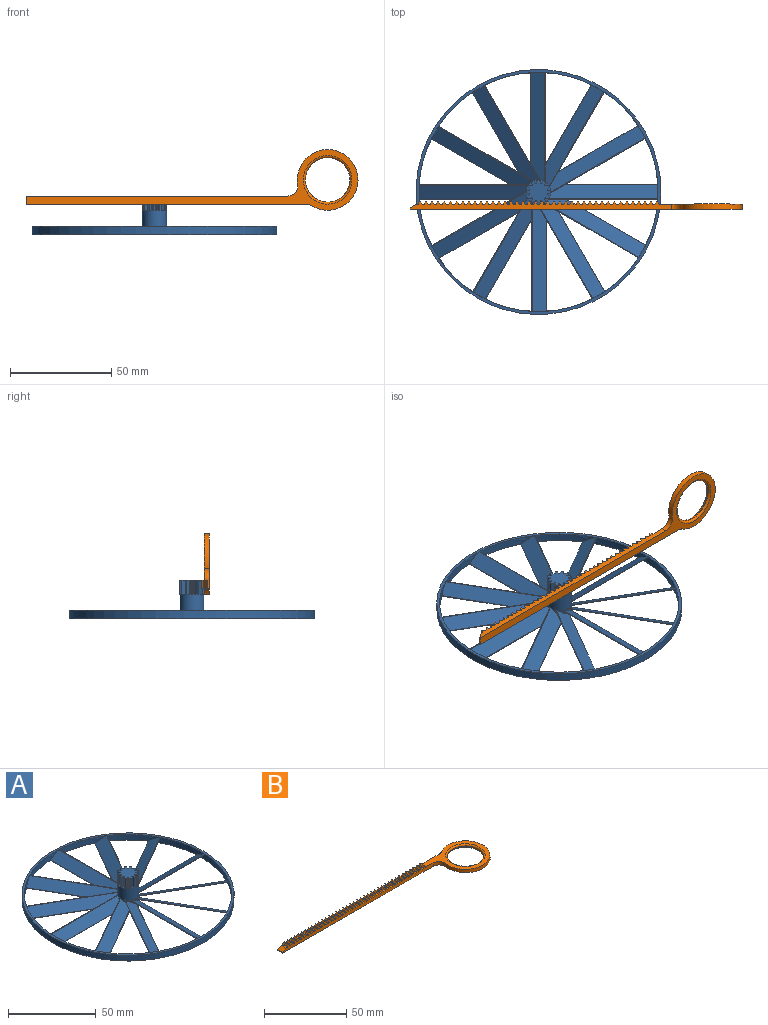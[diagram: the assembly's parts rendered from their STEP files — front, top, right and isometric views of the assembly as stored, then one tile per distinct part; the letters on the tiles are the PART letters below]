
ASSEMBLY  parts=2 mates=1
PART A: 92 faces, bbox 121.1x121.1x19.1 mm
  f0: plane 2.1x1.71mm, normal (0,0,1), area 2.1mm2, adj f12,f56,f59,f90
  f1: plane 1.96x1.96mm, normal (0,0,1), area 2.1mm2, adj f12,f87,f89,f91
  f2: plane 2.1x1.71mm, normal (0,0,1), area 2.1mm2, adj f12,f84,f86,f88
  f3: plane 2.1x1.71mm, normal (0,0,1), area 2.1mm2, adj f12,f81,f83,f85
  f4: plane 1.96x1.96mm, normal (0,0,1), area 2.1mm2, adj f12,f78,f80,f82
  f5: plane 2.1x1.71mm, normal (0,0,1), area 2.1mm2, adj f12,f75,f77,f79
  f6: plane 2.1x1.71mm, normal (0,0,1), area 2.1mm2, adj f12,f72,f74,f76
  f7: plane 1.96x1.96mm, normal (0,0,1), area 2.1mm2, adj f12,f69,f71,f73
  f8: plane 2.1x1.71mm, normal (0,0,1), area 2.1mm2, adj f12,f66,f68,f70
  f9: plane 2.1x1.71mm, normal (0,0,1), area 2.1mm2, adj f12,f63,f65,f67
  f10: plane 1.96x1.96mm, normal (0,0,1), area 2.1mm2, adj f12,f60,f62,f64
  f11: plane 2.1x1.71mm, normal (0,0,1), area 2.1mm2, adj f12,f55,f58,f61
  f12: cylinder r=6mm len=19mm, axis (0,0,-1), area 479.2mm2, adj f0,f1,f2,f3,f4,f5,f6,f7
  f13: cylinder r=6mm len=0.68mm, axis (0,0,-1), area 0.1mm2, adj f12,f16,f34
  f14: cylinder r=6mm len=3.6mm, axis (0,0,-1), area 2.4mm2, adj f12,f16,f35,f36
  f15: cylinder r=6mm len=5.58mm, axis (0,0,-1), area 6.1mm2, adj f12,f16,f37,f38
  f16: plane 121x121mm, normal (0,0,-1), area 866.8mm2, adj f12,f13,f14,f15,f17,f18,f19,f20
  f17: cylinder r=20mm len=54.2mm, axis (0,1,0), area 430.3mm2, adj f12,f16,f41,f54
  f18: plane 54.47x6.93mm, normal (0.5,0,0.87), area 427.4mm2, adj f12,f16,f42,f54
  f19: cylinder r=20mm len=50.4mm, axis (-0.5,0.87,0), area 430.3mm2, adj f12,f16,f42,f54
  f20: plane 50.1x33.19mm, normal (0.43,-0.25,0.87), area 427.4mm2, adj f12,f16,f41,f54
  f21: plane 50.57x32.93mm, normal (0.43,0.25,0.87), area 427.4mm2, adj f12,f16,f43,f54
  f22: cylinder r=20mm len=50.4mm, axis (-0.87,0.5,0), area 430.3mm2, adj f12,f16,f43,f54
  f23: plane 50.1x33.19mm, normal (0.25,0.43,0.87), area 427.4mm2, adj f12,f16,f44,f54
  f24: cylinder r=20mm len=54.2mm, axis (-1,0,0), area 430.3mm2, adj f12,f16,f44,f54
  f25: plane 54.47x6.93mm, normal (0,0.5,0.87), area 427.4mm2, adj f12,f16,f45,f54
  f26: cylinder r=20mm len=50.4mm, axis (-0.87,-0.5,0), area 430.3mm2, adj f12,f16,f45,f54
  f27: plane 50.57x32.93mm, normal (-0.25,0.43,0.87), area 427.4mm2, adj f12,f16,f46,f54
  f28: cylinder r=20mm len=50.4mm, axis (-0.5,-0.87,0), area 430.3mm2, adj f12,f16,f46,f54
  f29: plane 50.1x33.19mm, normal (-0.43,0.25,0.87), area 427.4mm2, adj f12,f16,f47,f54
  f30: cylinder r=20mm len=54.2mm, axis (0,-1,0), area 430.3mm2, adj f12,f16,f47,f54
  f31: plane 54.47x6.93mm, normal (-0.5,0,0.87), area 427.4mm2, adj f12,f16,f48,f54
  f32: cylinder r=20mm len=50.4mm, axis (0.5,-0.87,0), area 430.3mm2, adj f12,f16,f48,f54
  f33: plane 50.57x32.93mm, normal (-0.43,-0.25,0.87), area 427.4mm2, adj f12,f16,f49,f54
  f34: cylinder r=20mm len=50.4mm, axis (0.87,-0.5,0), area 430.3mm2, adj f12,f13,f16,f49,f54
  f35: plane 50.17x33.27mm, normal (-0.25,-0.43,0.87), area 427.4mm2, adj f12,f14,f16,f50,f54
  f36: cylinder r=20mm len=54.2mm, axis (1,0,0), area 430.3mm2, adj f12,f14,f16,f50,f54
  f37: plane 54.61x7.07mm, normal (0,-0.5,0.87), area 427.4mm2, adj f12,f15,f16,f51,f54
  f38: cylinder r=20mm len=50.4mm, axis (0.87,0.5,0), area 430.3mm2, adj f12,f15,f16,f51,f54
  f39: plane 50.57x32.93mm, normal (0.25,-0.43,0.87), area 427.4mm2, adj f12,f16,f52,f54
  f40: cylinder r=20mm len=50.4mm, axis (0.5,0.87,0), area 430.3mm2, adj f12,f16,f52,f54
  f41: cylinder r=59.1mm len=35.67mm, axis (0,0,-1), area 120.2mm2, adj f16,f17,f20,f54
  f42: cylinder r=59.1mm len=35.61mm, axis (0,0,-1), area 120.2mm2, adj f16,f18,f19,f54
  f43: cylinder r=59.1mm len=26.17mm, axis (0,0,-1), area 120.2mm2, adj f16,f21,f22,f54
  f44: cylinder r=59.1mm len=35.67mm, axis (0,0,-1), area 120.2mm2, adj f16,f23,f24,f54
  f45: cylinder r=59.1mm len=35.61mm, axis (0,0,-1), area 120.2mm2, adj f16,f25,f26,f54
  f46: cylinder r=59.1mm len=26.17mm, axis (0,0,-1), area 120.2mm2, adj f16,f27,f28,f54
  f47: cylinder r=59.1mm len=35.67mm, axis (0,0,-1), area 120.2mm2, adj f16,f29,f30,f54
  f48: cylinder r=59.1mm len=35.61mm, axis (0,0,-1), area 120.2mm2, adj f16,f31,f32,f54
  f49: cylinder r=59.1mm len=26.17mm, axis (0,0,-1), area 120.2mm2, adj f16,f33,f34,f54
  f50: cylinder r=59.1mm len=35.67mm, axis (0,0,-1), area 120.2mm2, adj f16,f35,f36,f54
  f51: cylinder r=59.1mm len=35.61mm, axis (0,0,-1), area 120.2mm2, adj f16,f37,f38,f54
  f52: cylinder r=59.1mm len=26.17mm, axis (0,0,-1), area 120.2mm2, adj f16,f39,f40,f54
  f53: cylinder r=60.5mm len=121mm, axis (0,0,-1), area 1520.5mm2, adj f16,f54
  f54: plane 121x121mm, normal (0,0,1), area 752.8mm2, adj f12,f17,f18,f19,f20,f21,f22,f23
  f55: plane 7x1.57mm, normal (-0.97,0.26,0), area 11.4mm2, adj f11,f12,f57,f58
  f56: plane 7x1.57mm, normal (0.97,0.26,0), area 11.4mm2, adj f0,f12,f57,f59
  f57: plane 12x12mm, normal (0,0,1), area 88.4mm2, adj f12,f55,f56,f58,f59,f60,f61,f62
  f58: cylinder r=4.5mm len=7mm, axis (0,0,-1), area 3.8mm2, adj f11,f55,f57,f61
  f59: cylinder r=4.5mm len=7mm, axis (0,0,-1), area 3.8mm2, adj f0,f56,f57,f90
  f60: plane 7x1.57mm, normal (-0.97,-0.26,0), area 11.4mm2, adj f10,f12,f57,f62
  f61: plane 7x1.15mm, normal (0.71,0.71,0), area 11.4mm2, adj f11,f12,f57,f58
  f62: cylinder r=4.5mm len=7mm, axis (0,0,-1), area 3.8mm2, adj f10,f57,f60,f64
  f63: plane 7x1.15mm, normal (-0.71,-0.71,0), area 11.4mm2, adj f9,f12,f57,f65
  f64: plane 7x1.57mm, normal (0.26,0.97,0), area 11.4mm2, adj f10,f12,f57,f62
  f65: cylinder r=4.5mm len=7mm, axis (0,0,-1), area 3.8mm2, adj f9,f57,f63,f67
  f66: plane 7x1.57mm, normal (-0.26,-0.97,0), area 11.4mm2, adj f8,f12,f57,f68
  f67: plane 7x1.57mm, normal (-0.26,0.97,0), area 11.4mm2, adj f9,f12,f57,f65
  f68: cylinder r=4.5mm len=7mm, axis (0,0,-1), area 3.8mm2, adj f8,f57,f66,f70
  f69: plane 7x1.57mm, normal (0.26,-0.97,0), area 11.4mm2, adj f7,f12,f57,f71
  f70: plane 7x1.15mm, normal (-0.71,0.71,0), area 11.4mm2, adj f8,f12,f57,f68
  f71: cylinder r=4.5mm len=7mm, axis (0,0,-1), area 3.8mm2, adj f7,f57,f69,f73
  f72: plane 7x1.15mm, normal (0.71,-0.71,0), area 11.4mm2, adj f6,f12,f57,f74
  f73: plane 7x1.57mm, normal (-0.97,0.26,0), area 11.4mm2, adj f7,f12,f57,f71
  f74: cylinder r=4.5mm len=7mm, axis (0,0,-1), area 3.8mm2, adj f6,f57,f72,f76
  f75: plane 7x1.57mm, normal (0.97,-0.26,0), area 11.4mm2, adj f5,f12,f57,f77
  f76: plane 7x1.57mm, normal (-0.97,-0.26,0), area 11.4mm2, adj f6,f12,f57,f74
  f77: cylinder r=4.5mm len=7mm, axis (0,0,-1), area 3.8mm2, adj f5,f57,f75,f79
  f78: plane 7x1.57mm, normal (0.97,0.26,0), area 11.4mm2, adj f4,f12,f57,f80
  f79: plane 7x1.15mm, normal (-0.71,-0.71,0), area 11.4mm2, adj f5,f12,f57,f77
  f80: cylinder r=4.5mm len=7mm, axis (0,0,-1), area 3.8mm2, adj f4,f57,f78,f82
  f81: plane 7x1.15mm, normal (0.71,0.71,0), area 11.4mm2, adj f3,f12,f57,f83
  f82: plane 7x1.57mm, normal (-0.26,-0.97,0), area 11.4mm2, adj f4,f12,f57,f80
  f83: cylinder r=4.5mm len=7mm, axis (0,0,-1), area 3.8mm2, adj f3,f57,f81,f85
  f84: plane 7x1.57mm, normal (0.26,0.97,0), area 11.4mm2, adj f2,f12,f57,f86
  f85: plane 7x1.57mm, normal (0.26,-0.97,0), area 11.4mm2, adj f3,f12,f57,f83
  f86: cylinder r=4.5mm len=7mm, axis (0,0,-1), area 3.8mm2, adj f2,f57,f84,f88
  f87: plane 7x1.57mm, normal (-0.26,0.97,0), area 11.4mm2, adj f1,f12,f57,f89
  f88: plane 7x1.15mm, normal (0.71,-0.71,0), area 11.4mm2, adj f2,f12,f57,f86
  f89: cylinder r=4.5mm len=7mm, axis (0,0,-1), area 3.8mm2, adj f1,f57,f87,f91
  f90: plane 7x1.15mm, normal (-0.71,0.71,0), area 11.4mm2, adj f0,f12,f57,f59
  f91: plane 7x1.57mm, normal (0.97,-0.26,0), area 11.4mm2, adj f1,f12,f57,f89
PART B: 252 faces, bbox 164x30x3.8 mm
  f0: plane 4x0.94mm, normal (-0.87,0,0.49), area 4.3mm2, adj f1,f6,f7,f8
  f1: plane 4x0.38mm, normal (-0.81,0,0.59), area 1.9mm2, adj f0,f7,f8,f243
  f2: plane 164.01x30mm, normal (0,0,-1), area 816.3mm2, adj f7,f8,f245,f246,f248,f250,f251
  f3: plane 4x1mm, normal (0,0,1), area 4mm2, adj f4,f7,f8,f10
  f4: plane 4x0.38mm, normal (0.81,0,0.59), area 1.9mm2, adj f3,f5,f7,f8
  f5: plane 4x0.94mm, normal (0.87,0,0.49), area 4.3mm2, adj f4,f6,f7,f8
  f6: plane 4x0.4mm, normal (0,0,1), area 1.6mm2, adj f0,f5,f7,f8
  f7: plane 129.23x3.82mm, normal (0,-1,0), area 380.9mm2, adj f0,f1,f2,f3,f4,f5,f6,f9
  f8: plane 138.47x3.82mm, normal (0,1,0), area 404mm2, adj f0,f1,f2,f3,f4,f5,f6,f9
  f9: plane 4x0.94mm, normal (-0.87,0,0.49), area 4.3mm2, adj f7,f8,f10,f14
  f10: plane 4x0.38mm, normal (-0.81,0,0.59), area 1.9mm2, adj f3,f7,f8,f9
  f11: plane 4x1mm, normal (0,0,1), area 4mm2, adj f7,f8,f12,f16
  f12: plane 4x0.38mm, normal (0.81,0,0.59), area 1.9mm2, adj f7,f8,f11,f13
  f13: plane 4x0.94mm, normal (0.87,0,0.49), area 4.3mm2, adj f7,f8,f12,f14
  f14: plane 4x0.4mm, normal (0,0,1), area 1.6mm2, adj f7,f8,f9,f13
  f15: plane 4x0.94mm, normal (-0.87,0,0.49), area 4.3mm2, adj f7,f8,f16,f20
  f16: plane 4x0.38mm, normal (-0.81,0,0.59), area 1.9mm2, adj f7,f8,f11,f15
  f17: plane 4x1mm, normal (0,0,1), area 4mm2, adj f7,f8,f18,f22
  f18: plane 4x0.38mm, normal (0.81,0,0.59), area 1.9mm2, adj f7,f8,f17,f19
  f19: plane 4x0.94mm, normal (0.87,0,0.49), area 4.3mm2, adj f7,f8,f18,f20
  f20: plane 4x0.4mm, normal (0,0,1), area 1.6mm2, adj f7,f8,f15,f19
  f21: plane 4x0.94mm, normal (-0.87,0,0.49), area 4.3mm2, adj f7,f8,f22,f26
  f22: plane 4x0.38mm, normal (-0.81,0,0.59), area 1.9mm2, adj f7,f8,f17,f21
  f23: plane 4x1mm, normal (0,0,1), area 4mm2, adj f7,f8,f24,f28
  f24: plane 4x0.38mm, normal (0.81,0,0.59), area 1.9mm2, adj f7,f8,f23,f25
  f25: plane 4x0.94mm, normal (0.87,0,0.49), area 4.3mm2, adj f7,f8,f24,f26
  f26: plane 4x0.4mm, normal (0,0,1), area 1.6mm2, adj f7,f8,f21,f25
  f27: plane 4x0.94mm, normal (-0.87,0,0.49), area 4.3mm2, adj f7,f8,f28,f32
  f28: plane 4x0.38mm, normal (-0.81,0,0.59), area 1.9mm2, adj f7,f8,f23,f27
  f29: plane 4x1mm, normal (0,0,1), area 4mm2, adj f7,f8,f30,f34
  f30: plane 4x0.38mm, normal (0.81,0,0.59), area 1.9mm2, adj f7,f8,f29,f31
  f31: plane 4x0.94mm, normal (0.87,0,0.49), area 4.3mm2, adj f7,f8,f30,f32
  f32: plane 4x0.4mm, normal (0,0,1), area 1.6mm2, adj f7,f8,f27,f31
  f33: plane 4x0.94mm, normal (-0.87,0,0.49), area 4.3mm2, adj f7,f8,f34,f38
  f34: plane 4x0.38mm, normal (-0.81,0,0.59), area 1.9mm2, adj f7,f8,f29,f33
  f35: plane 4x1mm, normal (0,0,1), area 4mm2, adj f7,f8,f36,f40
  f36: plane 4x0.38mm, normal (0.81,0,0.59), area 1.9mm2, adj f7,f8,f35,f37
  f37: plane 4x0.94mm, normal (0.87,0,0.49), area 4.3mm2, adj f7,f8,f36,f38
  f38: plane 4x0.4mm, normal (0,0,1), area 1.6mm2, adj f7,f8,f33,f37
  f39: plane 4x0.94mm, normal (-0.87,0,0.49), area 4.3mm2, adj f7,f8,f40,f44
  f40: plane 4x0.38mm, normal (-0.81,0,0.59), area 1.9mm2, adj f7,f8,f35,f39
  f41: plane 4x1mm, normal (0,0,1), area 4mm2, adj f7,f8,f42,f46
  f42: plane 4x0.38mm, normal (0.81,0,0.59), area 1.9mm2, adj f7,f8,f41,f43
  f43: plane 4x0.94mm, normal (0.87,0,0.49), area 4.3mm2, adj f7,f8,f42,f44
  f44: plane 4x0.4mm, normal (0,0,1), area 1.6mm2, adj f7,f8,f39,f43
  f45: plane 4x0.94mm, normal (-0.87,0,0.49), area 4.3mm2, adj f7,f8,f46,f50
  f46: plane 4x0.38mm, normal (-0.81,0,0.59), area 1.9mm2, adj f7,f8,f41,f45
  f47: plane 4x1mm, normal (0,0,1), area 4mm2, adj f7,f8,f48,f52
  f48: plane 4x0.38mm, normal (0.81,0,0.59), area 1.9mm2, adj f7,f8,f47,f49
  f49: plane 4x0.94mm, normal (0.87,0,0.49), area 4.3mm2, adj f7,f8,f48,f50
  f50: plane 4x0.4mm, normal (0,0,1), area 1.6mm2, adj f7,f8,f45,f49
  f51: plane 4x0.94mm, normal (-0.87,0,0.49), area 4.3mm2, adj f7,f8,f52,f56
  f52: plane 4x0.38mm, normal (-0.81,0,0.59), area 1.9mm2, adj f7,f8,f47,f51
  f53: plane 4x1mm, normal (0,0,1), area 4mm2, adj f7,f8,f54,f58
  f54: plane 4x0.38mm, normal (0.81,0,0.59), area 1.9mm2, adj f7,f8,f53,f55
  f55: plane 4x0.94mm, normal (0.87,0,0.49), area 4.3mm2, adj f7,f8,f54,f56
  f56: plane 4x0.4mm, normal (0,0,1), area 1.6mm2, adj f7,f8,f51,f55
  f57: plane 4x0.94mm, normal (-0.87,0,0.49), area 4.3mm2, adj f7,f8,f58,f62
  f58: plane 4x0.38mm, normal (-0.81,0,0.59), area 1.9mm2, adj f7,f8,f53,f57
  f59: plane 4x1mm, normal (0,0,1), area 4mm2, adj f7,f8,f60,f64
  f60: plane 4x0.38mm, normal (0.81,0,0.59), area 1.9mm2, adj f7,f8,f59,f61
  f61: plane 4x0.94mm, normal (0.87,0,0.49), area 4.3mm2, adj f7,f8,f60,f62
  f62: plane 4x0.4mm, normal (0,0,1), area 1.6mm2, adj f7,f8,f57,f61
  f63: plane 4x0.94mm, normal (-0.87,0,0.49), area 4.3mm2, adj f7,f8,f64,f68
  f64: plane 4x0.38mm, normal (-0.81,0,0.59), area 1.9mm2, adj f7,f8,f59,f63
  f65: plane 4x1mm, normal (0,0,1), area 4mm2, adj f7,f8,f66,f70
  f66: plane 4x0.38mm, normal (0.81,0,0.59), area 1.9mm2, adj f7,f8,f65,f67
  f67: plane 4x0.94mm, normal (0.87,0,0.49), area 4.3mm2, adj f7,f8,f66,f68
  f68: plane 4x0.4mm, normal (0,0,1), area 1.6mm2, adj f7,f8,f63,f67
  f69: plane 4x0.94mm, normal (-0.87,0,0.49), area 4.3mm2, adj f7,f8,f70,f74
  f70: plane 4x0.38mm, normal (-0.81,0,0.59), area 1.9mm2, adj f7,f8,f65,f69
  f71: plane 4x1mm, normal (0,0,1), area 4mm2, adj f7,f8,f72,f76
  f72: plane 4x0.38mm, normal (0.81,0,0.59), area 1.9mm2, adj f7,f8,f71,f73
  f73: plane 4x0.94mm, normal (0.87,0,0.49), area 4.3mm2, adj f7,f8,f72,f74
  f74: plane 4x0.4mm, normal (0,0,1), area 1.6mm2, adj f7,f8,f69,f73
  f75: plane 4x0.94mm, normal (-0.87,0,0.49), area 4.3mm2, adj f7,f8,f76,f80
  f76: plane 4x0.38mm, normal (-0.81,0,0.59), area 1.9mm2, adj f7,f8,f71,f75
  f77: plane 4x1mm, normal (0,0,1), area 4mm2, adj f7,f8,f78,f82
  f78: plane 4x0.38mm, normal (0.81,0,0.59), area 1.9mm2, adj f7,f8,f77,f79
  f79: plane 4x0.94mm, normal (0.87,0,0.49), area 4.3mm2, adj f7,f8,f78,f80
  f80: plane 4x0.4mm, normal (0,0,1), area 1.6mm2, adj f7,f8,f75,f79
  f81: plane 4x0.94mm, normal (-0.87,0,0.49), area 4.3mm2, adj f7,f8,f82,f86
  f82: plane 4x0.38mm, normal (-0.81,0,0.59), area 1.9mm2, adj f7,f8,f77,f81
  f83: plane 4x1mm, normal (0,0,1), area 4mm2, adj f7,f8,f84,f88
  f84: plane 4x0.38mm, normal (0.81,0,0.59), area 1.9mm2, adj f7,f8,f83,f85
  f85: plane 4x0.94mm, normal (0.87,0,0.49), area 4.3mm2, adj f7,f8,f84,f86
  f86: plane 4x0.4mm, normal (0,0,1), area 1.6mm2, adj f7,f8,f81,f85
  f87: plane 4x0.94mm, normal (-0.87,0,0.49), area 4.3mm2, adj f7,f8,f88,f92
  f88: plane 4x0.38mm, normal (-0.81,0,0.59), area 1.9mm2, adj f7,f8,f83,f87
  f89: plane 4x1mm, normal (0,0,1), area 4mm2, adj f7,f8,f90,f94
  f90: plane 4x0.38mm, normal (0.81,0,0.59), area 1.9mm2, adj f7,f8,f89,f91
  f91: plane 4x0.94mm, normal (0.87,0,0.49), area 4.3mm2, adj f7,f8,f90,f92
  f92: plane 4x0.4mm, normal (0,0,1), area 1.6mm2, adj f7,f8,f87,f91
  f93: plane 4x0.94mm, normal (-0.87,0,0.49), area 4.3mm2, adj f7,f8,f94,f98
  f94: plane 4x0.38mm, normal (-0.81,0,0.59), area 1.9mm2, adj f7,f8,f89,f93
  f95: plane 4x1mm, normal (0,0,1), area 4mm2, adj f7,f8,f96,f100
  f96: plane 4x0.38mm, normal (0.81,0,0.59), area 1.9mm2, adj f7,f8,f95,f97
  f97: plane 4x0.94mm, normal (0.87,0,0.49), area 4.3mm2, adj f7,f8,f96,f98
  f98: plane 4x0.4mm, normal (0,0,1), area 1.6mm2, adj f7,f8,f93,f97
  f99: plane 4x0.94mm, normal (-0.87,0,0.49), area 4.3mm2, adj f7,f8,f100,f104
  f100: plane 4x0.38mm, normal (-0.81,0,0.59), area 1.9mm2, adj f7,f8,f95,f99
  f101: plane 4x1mm, normal (0,0,1), area 4mm2, adj f7,f8,f102,f106
  f102: plane 4x0.38mm, normal (0.81,0,0.59), area 1.9mm2, adj f7,f8,f101,f103
  f103: plane 4x0.94mm, normal (0.87,0,0.49), area 4.3mm2, adj f7,f8,f102,f104
  f104: plane 4x0.4mm, normal (0,0,1), area 1.6mm2, adj f7,f8,f99,f103
  f105: plane 4x0.94mm, normal (-0.87,0,0.49), area 4.3mm2, adj f7,f8,f106,f110
  f106: plane 4x0.38mm, normal (-0.81,0,0.59), area 1.9mm2, adj f7,f8,f101,f105
  f107: plane 4x1mm, normal (0,0,1), area 4mm2, adj f7,f8,f108,f112
  f108: plane 4x0.38mm, normal (0.81,0,0.59), area 1.9mm2, adj f7,f8,f107,f109
  f109: plane 4x0.94mm, normal (0.87,0,0.49), area 4.3mm2, adj f7,f8,f108,f110
  f110: plane 4x0.4mm, normal (0,0,1), area 1.6mm2, adj f7,f8,f105,f109
  f111: plane 4x0.94mm, normal (-0.87,0,0.49), area 4.3mm2, adj f7,f8,f112,f116
  f112: plane 4x0.38mm, normal (-0.81,0,0.59), area 1.9mm2, adj f7,f8,f107,f111
  f113: plane 4x1mm, normal (0,0,1), area 4mm2, adj f7,f8,f114,f118
  f114: plane 4x0.38mm, normal (0.81,0,0.59), area 1.9mm2, adj f7,f8,f113,f115
  f115: plane 4x0.94mm, normal (0.87,0,0.49), area 4.3mm2, adj f7,f8,f114,f116
  f116: plane 4x0.4mm, normal (0,0,1), area 1.6mm2, adj f7,f8,f111,f115
  f117: plane 4x0.94mm, normal (-0.87,0,0.49), area 4.3mm2, adj f7,f8,f118,f122
  f118: plane 4x0.38mm, normal (-0.81,0,0.59), area 1.9mm2, adj f7,f8,f113,f117
  f119: plane 4x1mm, normal (0,0,1), area 4mm2, adj f7,f8,f120,f124
  f120: plane 4x0.38mm, normal (0.81,0,0.59), area 1.9mm2, adj f7,f8,f119,f121
  f121: plane 4x0.94mm, normal (0.87,0,0.49), area 4.3mm2, adj f7,f8,f120,f122
  f122: plane 4x0.4mm, normal (0,0,1), area 1.6mm2, adj f7,f8,f117,f121
  f123: plane 4x0.94mm, normal (-0.87,0,0.49), area 4.3mm2, adj f7,f8,f124,f128
  f124: plane 4x0.38mm, normal (-0.81,0,0.59), area 1.9mm2, adj f7,f8,f119,f123
  f125: plane 4x1mm, normal (0,0,1), area 4mm2, adj f7,f8,f126,f130
  f126: plane 4x0.38mm, normal (0.81,0,0.59), area 1.9mm2, adj f7,f8,f125,f127
  f127: plane 4x0.94mm, normal (0.87,0,0.49), area 4.3mm2, adj f7,f8,f126,f128
  f128: plane 4x0.4mm, normal (0,0,1), area 1.6mm2, adj f7,f8,f123,f127
  f129: plane 4x0.94mm, normal (-0.87,0,0.49), area 4.3mm2, adj f7,f8,f130,f134
  f130: plane 4x0.38mm, normal (-0.81,0,0.59), area 1.9mm2, adj f7,f8,f125,f129
  f131: plane 4x1mm, normal (0,0,1), area 4mm2, adj f7,f8,f132,f136
  f132: plane 4x0.38mm, normal (0.81,0,0.59), area 1.9mm2, adj f7,f8,f131,f133
  f133: plane 4x0.94mm, normal (0.87,0,0.49), area 4.3mm2, adj f7,f8,f132,f134
  f134: plane 4x0.4mm, normal (0,0,1), area 1.6mm2, adj f7,f8,f129,f133
  f135: plane 4x0.94mm, normal (-0.87,0,0.49), area 4.3mm2, adj f7,f8,f136,f140
  f136: plane 4x0.38mm, normal (-0.81,0,0.59), area 1.9mm2, adj f7,f8,f131,f135
  f137: plane 4x1mm, normal (0,0,1), area 4mm2, adj f7,f8,f138,f142
  f138: plane 4x0.38mm, normal (0.81,0,0.59), area 1.9mm2, adj f7,f8,f137,f139
  f139: plane 4x0.94mm, normal (0.87,0,0.49), area 4.3mm2, adj f7,f8,f138,f140
  f140: plane 4x0.4mm, normal (0,0,1), area 1.6mm2, adj f7,f8,f135,f139
  f141: plane 4x0.94mm, normal (-0.87,0,0.49), area 4.3mm2, adj f7,f8,f142,f146
  f142: plane 4x0.38mm, normal (-0.81,0,0.59), area 1.9mm2, adj f7,f8,f137,f141
  f143: plane 4x1mm, normal (0,0,1), area 4mm2, adj f7,f8,f144,f148
  f144: plane 4x0.38mm, normal (0.81,0,0.59), area 1.9mm2, adj f7,f8,f143,f145
  f145: plane 4x0.94mm, normal (0.87,0,0.49), area 4.3mm2, adj f7,f8,f144,f146
  f146: plane 4x0.4mm, normal (0,0,1), area 1.6mm2, adj f7,f8,f141,f145
  f147: plane 4x0.94mm, normal (-0.87,0,0.49), area 4.3mm2, adj f7,f8,f148,f152
  f148: plane 4x0.38mm, normal (-0.81,0,0.59), area 1.9mm2, adj f7,f8,f143,f147
  f149: plane 4x1mm, normal (0,0,1), area 4mm2, adj f7,f8,f150,f154
  f150: plane 4x0.38mm, normal (0.81,0,0.59), area 1.9mm2, adj f7,f8,f149,f151
  f151: plane 4x0.94mm, normal (0.87,0,0.49), area 4.3mm2, adj f7,f8,f150,f152
  f152: plane 4x0.4mm, normal (0,0,1), area 1.6mm2, adj f7,f8,f147,f151
  f153: plane 4x0.94mm, normal (-0.87,0,0.49), area 4.3mm2, adj f7,f8,f154,f158
  f154: plane 4x0.38mm, normal (-0.81,0,0.59), area 1.9mm2, adj f7,f8,f149,f153
  f155: plane 4x1mm, normal (0,0,1), area 4mm2, adj f7,f8,f156,f160
  f156: plane 4x0.38mm, normal (0.81,0,0.59), area 1.9mm2, adj f7,f8,f155,f157
  f157: plane 4x0.94mm, normal (0.87,0,0.49), area 4.3mm2, adj f7,f8,f156,f158
  f158: plane 4x0.4mm, normal (0,0,1), area 1.6mm2, adj f7,f8,f153,f157
  f159: plane 4x0.94mm, normal (-0.87,0,0.49), area 4.3mm2, adj f7,f8,f160,f164
  f160: plane 4x0.38mm, normal (-0.81,0,0.59), area 1.9mm2, adj f7,f8,f155,f159
  f161: plane 4x1mm, normal (0,0,1), area 4mm2, adj f7,f8,f162,f166
  f162: plane 4x0.38mm, normal (0.81,0,0.59), area 1.9mm2, adj f7,f8,f161,f163
  f163: plane 4x0.94mm, normal (0.87,0,0.49), area 4.3mm2, adj f7,f8,f162,f164
  f164: plane 4x0.4mm, normal (0,0,1), area 1.6mm2, adj f7,f8,f159,f163
  f165: plane 4x0.94mm, normal (-0.87,0,0.49), area 4.3mm2, adj f7,f8,f166,f170
  f166: plane 4x0.38mm, normal (-0.81,0,0.59), area 1.9mm2, adj f7,f8,f161,f165
  f167: plane 4x1mm, normal (0,0,1), area 4mm2, adj f7,f8,f168,f172
  f168: plane 4x0.38mm, normal (0.81,0,0.59), area 1.9mm2, adj f7,f8,f167,f169
  f169: plane 4x0.94mm, normal (0.87,0,0.49), area 4.3mm2, adj f7,f8,f168,f170
  f170: plane 4x0.4mm, normal (0,0,1), area 1.6mm2, adj f7,f8,f165,f169
  f171: plane 4x0.94mm, normal (-0.87,0,0.49), area 4.3mm2, adj f7,f8,f172,f176
  f172: plane 4x0.38mm, normal (-0.81,0,0.59), area 1.9mm2, adj f7,f8,f167,f171
  f173: plane 4x1mm, normal (0,0,1), area 4mm2, adj f7,f8,f174,f178
  f174: plane 4x0.38mm, normal (0.81,0,0.59), area 1.9mm2, adj f7,f8,f173,f175
  f175: plane 4x0.94mm, normal (0.87,0,0.49), area 4.3mm2, adj f7,f8,f174,f176
  f176: plane 4x0.4mm, normal (0,0,1), area 1.6mm2, adj f7,f8,f171,f175
  f177: plane 4x0.94mm, normal (-0.87,0,0.49), area 4.3mm2, adj f7,f8,f178,f182
  f178: plane 4x0.38mm, normal (-0.81,0,0.59), area 1.9mm2, adj f7,f8,f173,f177
  f179: plane 4x1mm, normal (0,0,1), area 4mm2, adj f7,f8,f180,f184
  f180: plane 4x0.38mm, normal (0.81,0,0.59), area 1.9mm2, adj f7,f8,f179,f181
  f181: plane 4x0.94mm, normal (0.87,0,0.49), area 4.3mm2, adj f7,f8,f180,f182
  f182: plane 4x0.4mm, normal (0,0,1), area 1.6mm2, adj f7,f8,f177,f181
  f183: plane 4x0.94mm, normal (-0.87,0,0.49), area 4.3mm2, adj f7,f8,f184,f188
  f184: plane 4x0.38mm, normal (-0.81,0,0.59), area 1.9mm2, adj f7,f8,f179,f183
  f185: plane 4x1mm, normal (0,0,1), area 4mm2, adj f7,f8,f186,f190
  f186: plane 4x0.38mm, normal (0.81,0,0.59), area 1.9mm2, adj f7,f8,f185,f187
  f187: plane 4x0.94mm, normal (0.87,0,0.49), area 4.3mm2, adj f7,f8,f186,f188
  f188: plane 4x0.4mm, normal (0,0,1), area 1.6mm2, adj f7,f8,f183,f187
  f189: plane 4x0.94mm, normal (-0.87,0,0.49), area 4.3mm2, adj f7,f8,f190,f194
  f190: plane 4x0.38mm, normal (-0.81,0,0.59), area 1.9mm2, adj f7,f8,f185,f189
  f191: plane 4x1mm, normal (0,0,1), area 4mm2, adj f7,f8,f192,f196
  f192: plane 4x0.38mm, normal (0.81,0,0.59), area 1.9mm2, adj f7,f8,f191,f193
  f193: plane 4x0.94mm, normal (0.87,0,0.49), area 4.3mm2, adj f7,f8,f192,f194
  f194: plane 4x0.4mm, normal (0,0,1), area 1.6mm2, adj f7,f8,f189,f193
  f195: plane 4x0.94mm, normal (-0.87,0,0.49), area 4.3mm2, adj f7,f8,f196,f200
  f196: plane 4x0.38mm, normal (-0.81,0,0.59), area 1.9mm2, adj f7,f8,f191,f195
  f197: plane 4x1mm, normal (0,0,1), area 4mm2, adj f7,f8,f198,f202
  f198: plane 4x0.38mm, normal (0.81,0,0.59), area 1.9mm2, adj f7,f8,f197,f199
  f199: plane 4x0.94mm, normal (0.87,0,0.49), area 4.3mm2, adj f7,f8,f198,f200
  f200: plane 4x0.4mm, normal (0,0,1), area 1.6mm2, adj f7,f8,f195,f199
  f201: plane 4x0.94mm, normal (-0.87,0,0.49), area 4.3mm2, adj f7,f8,f202,f206
  f202: plane 4x0.38mm, normal (-0.81,0,0.59), area 1.9mm2, adj f7,f8,f197,f201
  f203: plane 4x1mm, normal (0,0,1), area 4mm2, adj f7,f8,f204,f208
  f204: plane 4x0.38mm, normal (0.81,0,0.59), area 1.9mm2, adj f7,f8,f203,f205
  f205: plane 4x0.94mm, normal (0.87,0,0.49), area 4.3mm2, adj f7,f8,f204,f206
  f206: plane 4x0.4mm, normal (0,0,1), area 1.6mm2, adj f7,f8,f201,f205
  f207: plane 4x0.94mm, normal (-0.87,0,0.49), area 4.3mm2, adj f7,f8,f208,f212
  f208: plane 4x0.38mm, normal (-0.81,0,0.59), area 1.9mm2, adj f7,f8,f203,f207
  f209: plane 4x1mm, normal (0,0,1), area 4mm2, adj f7,f8,f210,f214
  f210: plane 4x0.38mm, normal (0.81,0,0.59), area 1.9mm2, adj f7,f8,f209,f211
  f211: plane 4x0.94mm, normal (0.87,0,0.49), area 4.3mm2, adj f7,f8,f210,f212
  f212: plane 4x0.4mm, normal (0,0,1), area 1.6mm2, adj f7,f8,f207,f211
  f213: plane 4x0.94mm, normal (-0.87,0,0.49), area 4.3mm2, adj f7,f8,f214,f218
  f214: plane 4x0.38mm, normal (-0.81,0,0.59), area 1.9mm2, adj f7,f8,f209,f213
  f215: plane 4x1mm, normal (0,0,1), area 4mm2, adj f7,f8,f216,f220
  f216: plane 4x0.38mm, normal (0.81,0,0.59), area 1.9mm2, adj f7,f8,f215,f217
  f217: plane 4x0.94mm, normal (0.87,0,0.49), area 4.3mm2, adj f7,f8,f216,f218
  f218: plane 4x0.4mm, normal (0,0,1), area 1.6mm2, adj f7,f8,f213,f217
  f219: plane 4x0.94mm, normal (-0.87,0,0.49), area 4.3mm2, adj f7,f8,f220,f224
  f220: plane 4x0.38mm, normal (-0.81,0,0.59), area 1.9mm2, adj f7,f8,f215,f219
  f221: plane 4x1mm, normal (0,0,1), area 4mm2, adj f7,f8,f222,f226
  f222: plane 4x0.38mm, normal (0.81,0,0.59), area 1.9mm2, adj f7,f8,f221,f223
  f223: plane 4x0.94mm, normal (0.87,0,0.49), area 4.3mm2, adj f7,f8,f222,f224
  f224: plane 4x0.4mm, normal (0,0,1), area 1.6mm2, adj f7,f8,f219,f223
  f225: plane 4x0.94mm, normal (-0.87,0,0.49), area 4.3mm2, adj f7,f8,f226,f230
  f226: plane 4x0.38mm, normal (-0.81,0,0.59), area 1.9mm2, adj f7,f8,f221,f225
  f227: plane 4x1mm, normal (0,0,1), area 4mm2, adj f7,f8,f228,f232
  f228: plane 4x0.38mm, normal (0.81,0,0.59), area 1.9mm2, adj f7,f8,f227,f229
  f229: plane 4x0.94mm, normal (0.87,0,0.49), area 4.3mm2, adj f7,f8,f228,f230
  f230: plane 4x0.4mm, normal (0,0,1), area 1.6mm2, adj f7,f8,f225,f229
  f231: plane 4x0.94mm, normal (-0.87,0,0.49), area 4.3mm2, adj f7,f8,f232,f236
  f232: plane 4x0.38mm, normal (-0.81,0,0.59), area 1.9mm2, adj f7,f8,f227,f231
  f233: plane 4x1mm, normal (0,0,1), area 4mm2, adj f7,f8,f234,f238
  f234: plane 4x0.38mm, normal (0.81,0,0.59), area 1.9mm2, adj f7,f8,f233,f235
  f235: plane 4x0.94mm, normal (0.87,0,0.49), area 4.3mm2, adj f7,f8,f234,f236
  f236: plane 4x0.4mm, normal (0,0,1), area 1.6mm2, adj f7,f8,f231,f235
  f237: plane 4x0.94mm, normal (-0.87,0,0.49), area 4.3mm2, adj f7,f8,f238,f242
  f238: plane 4x0.38mm, normal (-0.81,0,0.59), area 1.9mm2, adj f7,f8,f233,f237
  f239: plane 41x30mm, normal (0,0,1), area 324.3mm2, adj f7,f8,f240,f246,f249,f250,f251
  f240: plane 4x0.38mm, normal (0.81,0,0.59), area 1.9mm2, adj f7,f8,f239,f241
  f241: plane 4x0.94mm, normal (0.87,0,0.49), area 4.3mm2, adj f7,f8,f240,f242
  f242: plane 4x0.4mm, normal (0,0,1), area 1.6mm2, adj f7,f8,f237,f241
  f243: plane 4x1.01mm, normal (0,0,1), area 4mm2, adj f1,f7,f8,f244
  f244: plane 4x3mm, normal (-0.54,0,0.84), area 14.2mm2, adj f7,f8,f243,f245
  f245: plane 4x0.6mm, normal (-1,0,0), area 2.4mm2, adj f2,f7,f8,f244
  f246: cylinder r=15mm len=30mm, axis (0,0,1), area 203.2mm2, adj f2,f239,f250,f251
  f247: cylinder r=11mm len=22mm, axis (0,0,1), area 34.6mm2, adj f248,f249
  f248: torus R=12mm, axis (0,0,-1), area 112.2mm2, adj f2,f247
  f249: torus R=12mm, axis (0,0,1), area 112.2mm2, adj f239,f247
  f250: cylinder r=5mm len=2.63mm, axis (0,0,1), area 6.9mm2, adj f2,f8,f239,f246
  f251: cylinder r=5mm len=5.75mm, axis (0,0,1), area 21.5mm2, adj f2,f7,f239,f246
PLACE A t=(-19.68,-9.2,-0.35)mm
PLACE B rot(axis=(-1,0,0),90deg) t=(-76.15,-17.7,14.65)mm
MATE planar A.f12 <-> B.f7  axis (0,0,1) through (-19.68,-9.2,18.65)mm
